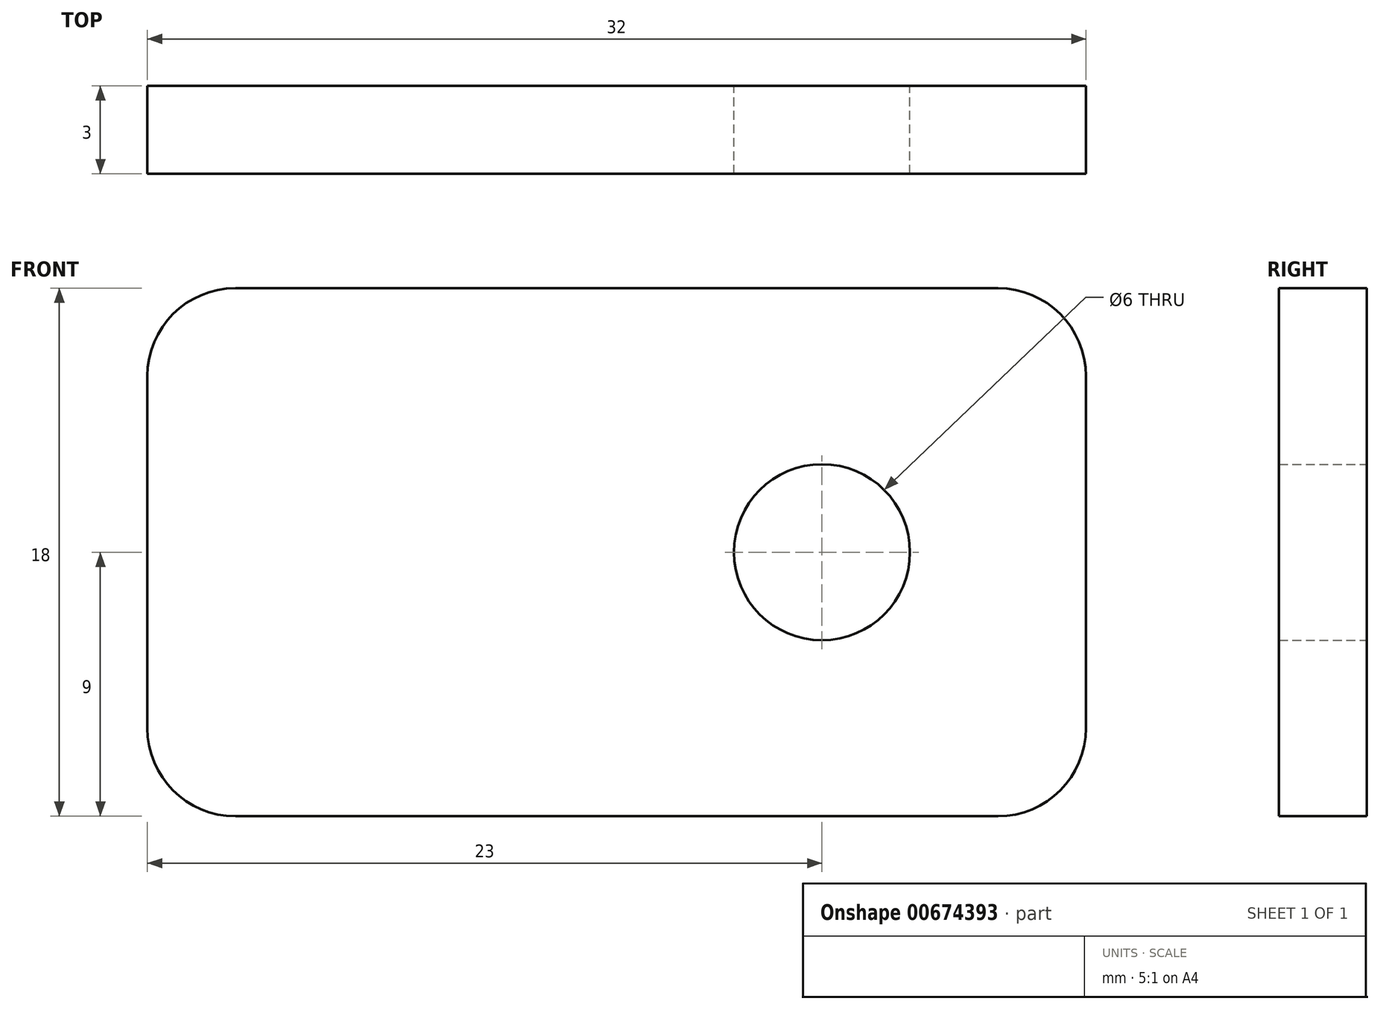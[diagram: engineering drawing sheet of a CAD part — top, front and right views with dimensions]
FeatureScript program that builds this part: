
annotation { "Feature Type Name" : "Feature", "Feature Type Description" : "" }
export const myFeature = defineFeature(function(context is Context, id is Id, definition is map)
    precondition{}
    {
        {
            var Q0;
            Q0=qCreatedBy(makeId("Front.planeOp"),FACE);
            var sketch = newSketch(context, id + "F0", { "sketchPlane" : qUnion([Q0])});
            skLineSegment(sketch, "E0.bottom", {"start": v(13, -9) * mm, "end": v(-13, -9) * mm});
            skLineSegment(sketch, "E0.top", {"start": v(13, 9) * mm, "end": v(-13, 9) * mm});
            skLineSegment(sketch, "E0.left", {"start": v(16, -6) * mm, "end": v(16, 6) * mm});
            skLineSegment(sketch, "E0.right", {"start": v(-16, -6) * mm, "end": v(-16, 6) * mm});
            skPoint(sketch, "E0.middle", {"position": v(0, 0) * mm});
            skCircle(sketch, "E1", {"center": v(7, 0) * mm, "radius": 3 * mm});
            skPoint(sketch, "E2.visualSharp", {"position": v(-16, 9) * mm});
            skArc(sketch, "E2.filletArc", {"start": v(-13, 9) * mm, "mid": v(-15.12, 8.12) * mm, "end": v(-16, 6) * mm});
            skPoint(sketch, "E3.visualSharp", {"position": v(-16, -9) * mm});
            skArc(sketch, "E3.filletArc", {"start": v(-16, -6) * mm, "mid": v(-15.12, -8.12) * mm, "end": v(-13, -9) * mm});
            skPoint(sketch, "E4.visualSharp", {"position": v(16, -9) * mm});
            skArc(sketch, "E4.filletArc", {"start": v(13, -9) * mm, "mid": v(15.12, -8.12) * mm, "end": v(16, -6) * mm});
            skPoint(sketch, "E5.visualSharp", {"position": v(16, 9) * mm});
            skArc(sketch, "E5.filletArc", {"start": v(16, 6) * mm, "mid": v(15.12, 8.12) * mm, "end": v(13, 9) * mm});
            skSolve(sketch);
        }
        {
            var Q0;
            Q0=makeQuery(id+"F0.imprint","IMPRINT",FACE,{"disambiguationData":[TD([[makeQuery(id+"F0.imprint","IMPRINT",EDGE,{"derivedFrom":sQuery(id+"F0.wireOp",EDGE,"E0.bottom")}),-1.0]])]});
            extrude(context, id + "F1", {"entities" : qUnion([Q0]), "depth" : 3 * mm, "offsetDistance" : 25 * mm});
        }
    });
